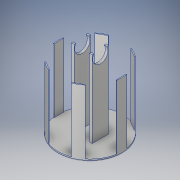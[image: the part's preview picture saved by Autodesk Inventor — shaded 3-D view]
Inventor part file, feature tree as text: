
AUTODESK INVENTOR PART (.ipt)
format: ipt  version: 2018 (Build 220112000, 112)  size: 178,176 bytes
history: native  units: in
note: dims shown in document units (in); Inventor stores cm internally (conversion verified against a paired STEP export)
features: extrude x4, sketch x4, fillet x1
ambient origin geometry x8: Origin, YZ Plane, XZ Plane, XY Plane, X Axis, Y Axis, Z Axis, Center Point
bodies: Solid1 (feature_tree)
feature tree (9):
  extrude  "Extrusion1"  Depth=0.013in TaperAngle=0.0deg
  extrude  "Extrusion2"  Depth=0.312in TaperAngle=360.0deg
  fillet  "Fillet1"  Radius=0.312in
  extrude  "Extrusion3"  Depth=0.013in
  extrude  "Extrusion4"  Depth=0.075in
  sketch  "Sketch1"  dims[d0=0.314in d1=0.013in d2=0.0in]
  sketch  "Sketch2"  dims[d3=90.0deg d4=2.3622in d6=360.0deg d8=0.312in d9=0.0in]
  sketch  "Sketch3"  dims[d10=0.0075in d11=0.013in]
  sketch  "Sketch5"  dims[d12=0.08in d13=0.04in d14=0.0375in d15=0.375in d16=0.0in d18=0.075in d19=0.35in d20=0.0in]
